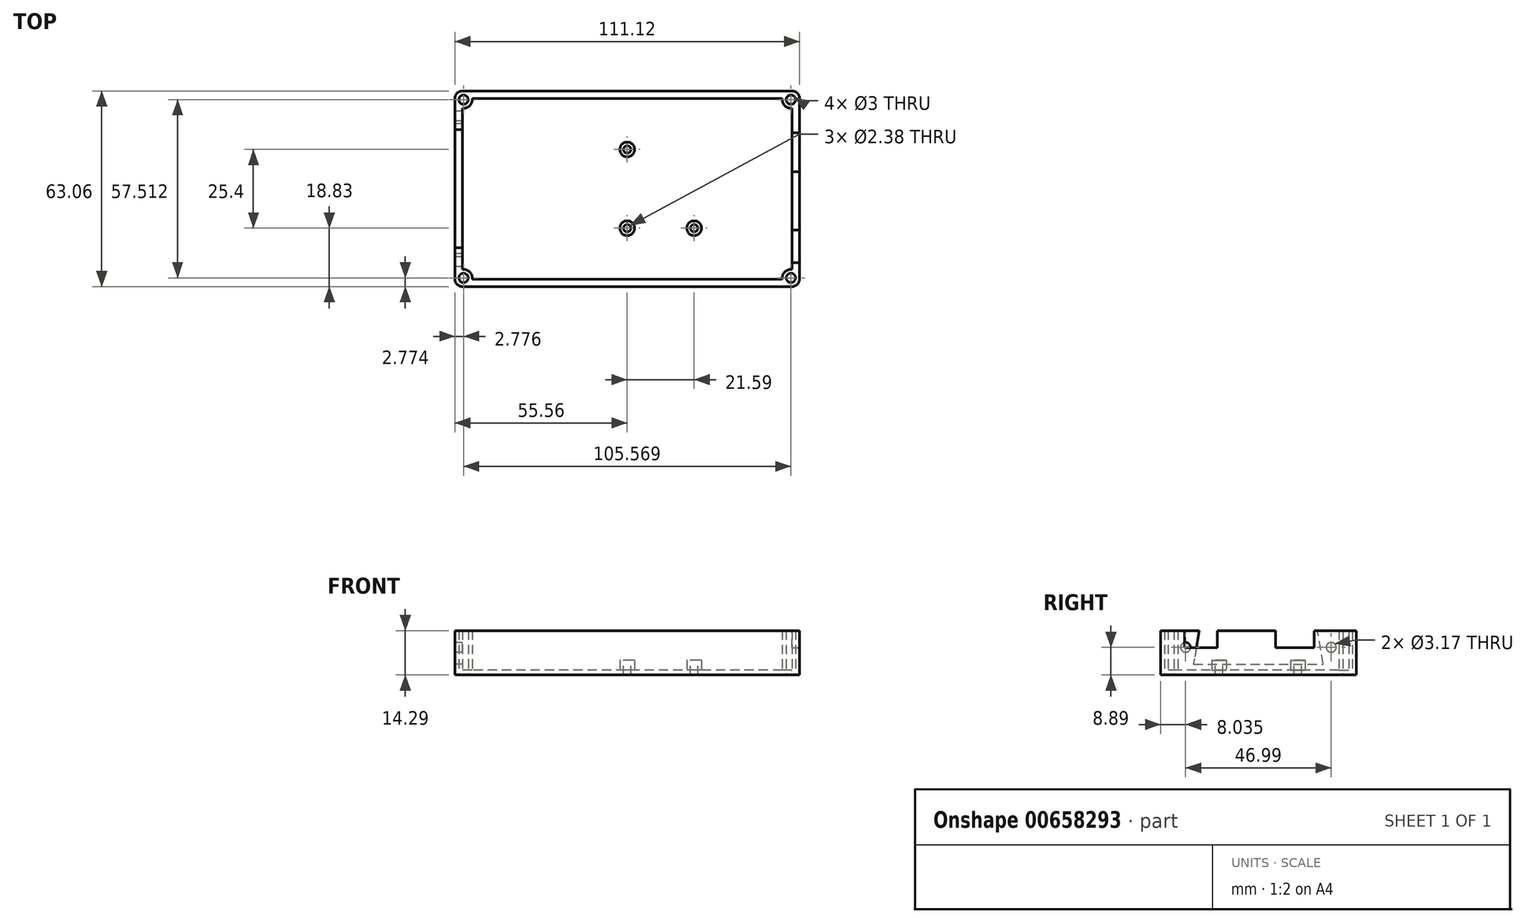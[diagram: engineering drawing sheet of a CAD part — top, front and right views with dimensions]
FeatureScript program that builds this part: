
annotation { "Feature Type Name" : "Feature", "Feature Type Description" : "" }
export const myFeature = defineFeature(function(context is Context, id is Id, definition is map)
    precondition{}
    {
        {
            var Q0;
            Q0=qCreatedBy(makeId("Top.planeOp"),FACE);
            var sketch = newSketch(context, id + "F0", { "sketchPlane" : qUnion([Q0])});
            skLineSegment(sketch, "E0.bottom", {"start": v(50.8, 26.77) * mm, "end": v(-50.8, 26.77) * mm});
            skLineSegment(sketch, "E0.top", {"start": v(50.8, -26.77) * mm, "end": v(-50.8, -26.77) * mm});
            skLineSegment(sketch, "E0.left", {"start": v(50.8, 26.77) * mm, "end": v(50.8, -26.77) * mm});
            skLineSegment(sketch, "E0.right", {"start": v(-50.8, 26.77) * mm, "end": v(-50.8, -26.77) * mm});
            skPoint(sketch, "E0.middle", {"position": v(0, 0) * mm});
            skSolve(sketch);
        }
        {
            var Q0;
            Q0=qCreatedBy(makeId("Top.planeOp"),FACE);
            var sketch = newSketch(context, id + "F1", { "sketchPlane" : qUnion([Q0])});
            skLineSegment(sketch, "E1.bottom", {"start": v(55.56, 31.53) * mm, "end": v(-55.56, 31.53) * mm});
            skLineSegment(sketch, "E1.top", {"start": v(55.56, -31.53) * mm, "end": v(-55.56, -31.53) * mm});
            skLineSegment(sketch, "E1.left", {"start": v(55.56, 31.53) * mm, "end": v(55.56, -31.53) * mm});
            skLineSegment(sketch, "E1.right", {"start": v(-55.56, 31.53) * mm, "end": v(-55.56, -31.53) * mm});
            skPoint(sketch, "E1.middle", {"position": v(0, 0) * mm});
            skLineSegment(sketch, "E2.bottom", {"start": v(53.97, 29.95) * mm, "end": v(-53.98, 29.95) * mm, "construction": true});
            skLineSegment(sketch, "E2.top", {"start": v(53.98, -29.95) * mm, "end": v(-53.97, -29.95) * mm, "construction": true});
            skLineSegment(sketch, "E2.left", {"start": v(53.97, 29.95) * mm, "end": v(53.98, -29.95) * mm, "construction": true});
            skLineSegment(sketch, "E2.right", {"start": v(-53.98, 29.95) * mm, "end": v(-53.97, -29.95) * mm, "construction": true});
            skSolve(sketch);
        }
        {
            var Q0;
            Q0=makeQuery(id+"F1.imprint","IMPRINT",FACE,{"disambiguationData":[TD([[makeQuery(id+"F1.imprint","IMPRINT",EDGE,{"derivedFrom":sQuery(id+"F1.wireOp",EDGE,"E1.bottom")}),1.0]])]});
            extrude(context, id + "F2", {"entities" : qUnion([Q0]), "depth" : 1.59 * mm, "offsetDistance" : 25.4 * mm});
        }
        {
            var Q0;
            Q0=makeQuery(id+"F2.opExtrude","CAP_FACE",FACE,{"disambiguationData":[OSD([sQuery(id+"F1.wireOp",EDGE,"E1.bottom"),sQuery(id+"F1.wireOp",EDGE,"E1.top"),sQuery(id+"F1.wireOp",EDGE,"E1.left"),sQuery(id+"F1.wireOp",EDGE,"E1.right")])],"isStart":false});
            var sketch = newSketch(context, id + "F3", { "sketchPlane" : qUnion([Q0])});
            skLineSegment(sketch, "E3.bottom", {"start": v(55.56, 31.53) * mm, "end": v(-55.56, 31.53) * mm});
            skLineSegment(sketch, "E3.top", {"start": v(55.56, -31.53) * mm, "end": v(-55.56, -31.53) * mm});
            skLineSegment(sketch, "E3.left", {"start": v(55.56, 31.53) * mm, "end": v(55.56, -31.53) * mm});
            skLineSegment(sketch, "E3.right", {"start": v(-55.56, 31.53) * mm, "end": v(-55.56, -31.53) * mm});
            skPoint(sketch, "E3.middle", {"position": v(0, 0) * mm});
            skLineSegment(sketch, "E4.left", {"start": v(53.18, 25.98) * mm, "end": v(53.18, -25.98) * mm});
            skLineSegment(sketch, "E4.right", {"start": v(-53.18, 25.98) * mm, "end": v(-53.18, -25.98) * mm});
            skArc(sketch, "E5", {"start": v(-52.78, 25.98) * mm, "mid": v(-50.82, 26.8) * mm, "end": v(-50, 28.76) * mm});
            skCircle(sketch, "E6", {"center": v(-52.78, 28.76) * mm, "radius": 1.5 * mm});
            skLineSegment(sketch, "E7", {"start": v(-50, 28.76) * mm, "end": v(-50, 29.15) * mm});
            skLineSegment(sketch, "E8", {"start": v(-52.78, 25.98) * mm, "end": v(-53.18, 25.98) * mm});
            skLineSegment(sketch, "E9", {"start": v(-55.56, 31.53) * mm, "end": v(-50.82, 26.8) * mm, "construction": true});
            skPoint(sketch, "E10", {"position": v(-53.2, 29.16) * mm});
            skPoint(sketch, "E11.orphan", {"position": v(-53.18, 37.1) * mm});
            skCircle(sketch, "E12.MirrorC", {"center": v(-52.78, -28.76) * mm, "radius": 1.5 * mm});
            skLineSegment(sketch, "E13.MirrorCS", {"start": v(-52.78, -25.98) * mm, "end": v(-53.18, -25.98) * mm});
            skArc(sketch, "E14.MirrorCS", {"start": v(-52.78, -25.98) * mm, "mid": v(-50.82, -26.8) * mm, "end": v(-50, -28.76) * mm});
            skLineSegment(sketch, "E15.MirrorCS", {"start": v(-50, -28.76) * mm, "end": v(-50, -29.15) * mm});
            skCircle(sketch, "E16.MirrorC", {"center": v(52.78, 28.76) * mm, "radius": 1.5 * mm});
            skLineSegment(sketch, "E17.MirrorCS", {"start": v(50, 28.76) * mm, "end": v(50, 29.15) * mm});
            skArc(sketch, "E18.MirrorCS", {"start": v(52.78, 25.98) * mm, "mid": v(50.82, 26.8) * mm, "end": v(50, 28.76) * mm});
            skLineSegment(sketch, "E19.MirrorCS", {"start": v(52.78, 25.98) * mm, "end": v(53.18, 25.98) * mm});
            skCircle(sketch, "E20.MirrorC", {"center": v(52.78, -28.76) * mm, "radius": 1.5 * mm});
            skLineSegment(sketch, "E21.MirrorCS", {"start": v(52.78, -25.98) * mm, "end": v(53.18, -25.98) * mm});
            skArc(sketch, "E22.MirrorCS", {"start": v(52.78, -25.98) * mm, "mid": v(50.82, -26.8) * mm, "end": v(50, -28.76) * mm});
            skLineSegment(sketch, "E23.MirrorCS", {"start": v(50, -28.76) * mm, "end": v(50, -29.15) * mm});
            skPoint(sketch, "E24.orphan", {"position": v(-53.18, -36.9) * mm});
            skLineSegment(sketch, "E25.trimOffspring", {"start": v(50, -29.15) * mm, "end": v(-50, -29.15) * mm});
            skPoint(sketch, "E26.orphan", {"position": v(53.18, -37.1) * mm});
            skLineSegment(sketch, "E27.trimOffspring", {"start": v(50, 29.15) * mm, "end": v(-50, 29.15) * mm});
            skPoint(sketch, "E28.orphan", {"position": v(53.18, 36.9) * mm});
            skSolve(sketch);
        }
        {
            var Q0;
            Q0=qSketchRegion(id+"F3",true);
            extrude(context, id + "F4", {"entities" : qUnion([Q0]), "operationType" : NewBodyOperationType.ADD, "depth" : 12.7 * mm, "offsetDistance" : 25.4 * mm});
        }
        {
            var Q0;
            Q0=makeQuery(id+"F4.boolean.opBoolean","MERGE",EDGE,{"derivedFrom":[makeQuery(id+"F2.opExtrude","SWEPT_EDGE",EDGE,{"disambiguationData":[OSD([sQuery(id+"F1.wireOp",EDGE,"E1.top"),sQuery(id+"F1.wireOp",EDGE,"E1.left")])]}),makeQuery(id+"F4.opExtrude","SWEPT_EDGE",EDGE,{"disambiguationData":[OSD([sQuery(id+"F3.wireOp",EDGE,"E3.top"),sQuery(id+"F3.wireOp",EDGE,"E3.left")])]})]});
            var Q1;
            Q1=makeQuery(id+"F4.boolean.opBoolean","MERGE",EDGE,{"derivedFrom":[makeQuery(id+"F2.opExtrude","SWEPT_EDGE",EDGE,{"disambiguationData":[OSD([sQuery(id+"F1.wireOp",EDGE,"E1.bottom"),sQuery(id+"F1.wireOp",EDGE,"E1.left")])]}),makeQuery(id+"F4.opExtrude","SWEPT_EDGE",EDGE,{"disambiguationData":[OSD([sQuery(id+"F3.wireOp",EDGE,"E3.bottom"),sQuery(id+"F3.wireOp",EDGE,"E3.left")])]})]});
            var Q2;
            Q2=makeQuery(id+"F4.boolean.opBoolean","MERGE",EDGE,{"derivedFrom":[makeQuery(id+"F2.opExtrude","SWEPT_EDGE",EDGE,{"disambiguationData":[OSD([sQuery(id+"F1.wireOp",EDGE,"E1.top"),sQuery(id+"F1.wireOp",EDGE,"E1.right")])]}),makeQuery(id+"F4.opExtrude","SWEPT_EDGE",EDGE,{"disambiguationData":[OSD([sQuery(id+"F3.wireOp",EDGE,"E3.top"),sQuery(id+"F3.wireOp",EDGE,"E3.right")])]})]});
            var Q3;
            Q3=makeQuery(id+"F4.boolean.opBoolean","MERGE",EDGE,{"derivedFrom":[makeQuery(id+"F2.opExtrude","SWEPT_EDGE",EDGE,{"disambiguationData":[OSD([sQuery(id+"F1.wireOp",EDGE,"E1.bottom"),sQuery(id+"F1.wireOp",EDGE,"E1.right")])]}),makeQuery(id+"F4.opExtrude","SWEPT_EDGE",EDGE,{"disambiguationData":[OSD([sQuery(id+"F3.wireOp",EDGE,"E3.bottom"),sQuery(id+"F3.wireOp",EDGE,"E3.right")])]})]});
            fillet(context, id + "F5", {"entities" : qUnion([Q0, Q1, Q2, Q3]), "radius" : 2.38 * mm, "tangentPropagation" : true, "allowEdgeOverflow" : false});
        }
        {
            var Q0;
            Q0=makeQuery(id+"F4.boolean.opBoolean","MERGE",FACE,{"derivedFrom":[makeQuery(id+"F2.opExtrude","SWEPT_FACE",FACE,{"disambiguationData":[OSD([sQuery(id+"F1.wireOp",EDGE,"E1.left")])]}),makeQuery(id+"F4.opExtrude","SWEPT_FACE",FACE,{"disambiguationData":[OSD([sQuery(id+"F3.wireOp",EDGE,"E3.left")])]})]});
            var sketch = newSketch(context, id + "F6", { "sketchPlane" : qUnion([Q0])});
            skLineSegment(sketch, "E29.bottom", {"start": v(-23.77, 14.29) * mm, "end": v(-13.27, 14.29) * mm});
            skLineSegment(sketch, "E29.top", {"start": v(-23.77, 8.76) * mm, "end": v(-13.27, 8.76) * mm});
            skLineSegment(sketch, "E29.left", {"start": v(-23.77, 14.29) * mm, "end": v(-23.77, 8.76) * mm});
            skLineSegment(sketch, "E29.right", {"start": v(-13.27, 14.29) * mm, "end": v(-13.27, 8.76) * mm});
            skLineSegment(sketch, "E30.bottom", {"start": v(5.52, 14.29) * mm, "end": v(18.02, 14.29) * mm});
            skLineSegment(sketch, "E30.top", {"start": v(5.52, 8.76) * mm, "end": v(18.02, 8.76) * mm});
            skLineSegment(sketch, "E30.left", {"start": v(5.52, 14.29) * mm, "end": v(5.52, 8.76) * mm});
            skLineSegment(sketch, "E30.right", {"start": v(18.02, 14.29) * mm, "end": v(18.02, 8.76) * mm});
            skLineSegment(sketch, "E31", {"start": v(-26.77, 14.29) * mm, "end": v(-26.77, 0) * mm, "construction": true});
            skLineSegment(sketch, "E32.MirrorCS", {"start": v(26.77, 14.29) * mm, "end": v(26.77, 0) * mm, "construction": true});
            skPoint(sketch, "E33", {"position": v(11.77, 8.76) * mm});
            skSolve(sketch);
        }
        {
            var Q0;
            Q0=qSketchRegion(id+"F6",true);
            extrude(context, id + "F7", {"entities" : qUnion([Q0]), "operationType" : NewBodyOperationType.REMOVE, "endBound" : BoundingType.UP_TO_NEXT, "oppositeDirection" : true, "depth" : 25.4 * mm, "offsetDistance" : 25.4 * mm});
        }
        {
            var Q0;
            Q0=makeQuery(id+"F0.imprint","IMPRINT",FACE,{"disambiguationData":[TD([[makeQuery(id+"F0.imprint","IMPRINT",EDGE,{"derivedFrom":sQuery(id+"F0.wireOp",EDGE,"E0.bottom")}),1.0]])]});
            var sketch = newSketch(context, id + "F8", { "sketchPlane" : qUnion([Q0])});
            skLineSegment(sketch, "E34.bottom", {"start": v(-42.55, -25.36) * mm, "end": v(33.02, -25.36) * mm});
            skLineSegment(sketch, "E34.top", {"start": v(-42.55, -22.18) * mm, "end": v(33.02, -22.18) * mm});
            skLineSegment(sketch, "E34.left", {"start": v(-42.55, -25.36) * mm, "end": v(-42.55, -22.18) * mm});
            skLineSegment(sketch, "E34.right", {"start": v(33.02, -25.36) * mm, "end": v(33.02, -22.18) * mm});
            skPoint(sketch, "E35", {"position": v(-42.55, -23.77) * mm});
            skLineSegment(sketch, "E36.MirrorCS", {"start": v(33.02, 25.36) * mm, "end": v(33.02, 22.18) * mm});
            skLineSegment(sketch, "E37.MirrorCS", {"start": v(-42.55, 25.36) * mm, "end": v(-42.55, 22.18) * mm});
            skLineSegment(sketch, "E38.MirrorCS", {"start": v(-42.55, 22.18) * mm, "end": v(33.02, 22.18) * mm});
            skLineSegment(sketch, "E39.MirrorCS", {"start": v(-42.55, 25.36) * mm, "end": v(33.02, 25.36) * mm});
            skPoint(sketch, "E40.MirrorP", {"position": v(-42.55, 23.77) * mm});
            skSolve(sketch);
        }
        {
            var Q0;
            Q0=makeQuery(id+"F4.boolean.opBoolean","MERGE",FACE,{"derivedFrom":[makeQuery(id+"F2.opExtrude","SWEPT_FACE",FACE,{"disambiguationData":[OSD([sQuery(id+"F1.wireOp",EDGE,"E1.right")])]}),makeQuery(id+"F4.opExtrude","SWEPT_FACE",FACE,{"disambiguationData":[OSD([sQuery(id+"F3.wireOp",EDGE,"E3.right")])]})]});
            var sketch = newSketch(context, id + "F9", { "sketchPlane" : qUnion([Q0])});
            skLineSegment(sketch, "E41", {"start": v(-19.05, 14.29) * mm, "end": v(19.05, 14.29) * mm});
            skLineSegment(sketch, "E42", {"start": v(19.05, 14.29) * mm, "end": v(20.95, 3.5) * mm});
            skLineSegment(sketch, "E43", {"start": v(20.95, 3.5) * mm, "end": v(-20.96, 3.5) * mm});
            skLineSegment(sketch, "E44", {"start": v(-20.96, 3.5) * mm, "end": v(-19.05, 14.29) * mm});
            skPoint(sketch, "E45", {"position": v(0, 14.29) * mm});
            skPoint(sketch, "E46", {"position": v(0, 3.5) * mm});
            skCircle(sketch, "E47", {"center": v(-23.5, 8.9) * mm, "radius": 1.59 * mm});
            skCircle(sketch, "E48", {"center": v(23.5, 8.9) * mm, "radius": 1.59 * mm});
            skLineSegment(sketch, "E49", {"start": v(0, 14.29) * mm, "end": v(0, 3.5) * mm, "construction": true});
            skPoint(sketch, "E50", {"position": v(0, 8.89) * mm});
            skSolve(sketch);
        }
        {
            var Q0;
            Q0=qSketchRegion(id+"F9",true);
            extrude(context, id + "F10", {"entities" : qUnion([Q0]), "operationType" : NewBodyOperationType.REMOVE, "endBound" : BoundingType.UP_TO_NEXT, "oppositeDirection" : true, "depth" : 25.4 * mm, "offsetDistance" : 25.4 * mm});
        }
        {
            var Q0;
            Q0=makeQuery(id+"F4.boolean.opBoolean","SPLIT",FACE,{"disambiguationData":[TD([makeQuery(id+"F4.opExtrude","SWEPT_FACE",FACE,{"disambiguationData":[OSD([sQuery(id+"F3.wireOp",EDGE,"E4.left")])]})])],"derivedFrom":makeQuery(id+"F2.opExtrude","CAP_FACE",FACE,{"disambiguationData":[OSD([sQuery(id+"F1.wireOp",EDGE,"E1.bottom"),sQuery(id+"F1.wireOp",EDGE,"E1.top"),sQuery(id+"F1.wireOp",EDGE,"E1.left"),sQuery(id+"F1.wireOp",EDGE,"E1.right")])],"isStart":false})});
            var sketch = newSketch(context, id + "F11", { "sketchPlane" : qUnion([Q0])});
            skCircle(sketch, "E51", {"center": v(0, 12.7) * mm, "radius": 2.38 * mm});
            skCircle(sketch, "E52.MirrorC", {"center": v(0, -12.7) * mm, "radius": 2.38 * mm});
            skCircle(sketch, "E53", {"center": v(21.59, -12.7) * mm, "radius": 2.38 * mm});
            skSolve(sketch);
        }
        {
            var Q0;
            Q0=qSketchRegion(id+"F11",true);
            extrude(context, id + "F12", {"entities" : qUnion([Q0]), "operationType" : NewBodyOperationType.ADD, "depth" : 3.17 * mm, "offsetDistance" : 25.4 * mm});
        }
        {
            var Q0;
            Q0=makeQuery(id+"F12.opExtrude","CAP_FACE",FACE,{"disambiguationData":[OSD([sQuery(id+"F11.wireOp",EDGE,"E51")])],"isStart":false});
            var sketch = newSketch(context, id + "F13", { "sketchPlane" : qUnion([Q0])});
            skCircle(sketch, "E54", {"center": v(0, 12.7) * mm, "radius": 1.2 * mm});
            skCircle(sketch, "E55.MirrorC", {"center": v(0, -12.7) * mm, "radius": 1.2 * mm});
            skCircle(sketch, "E56", {"center": v(21.59, -12.7) * mm, "radius": 1.2 * mm});
            skSolve(sketch);
        }
        {
            var Q0;
            Q0=qSketchRegion(id+"F13",true);
            extrude(context, id + "F14", {"entities" : qUnion([Q0]), "operationType" : NewBodyOperationType.REMOVE, "endBound" : BoundingType.THROUGH_ALL, "oppositeDirection" : true, "depth" : 25.4 * mm, "offsetDistance" : 25.4 * mm});
        }
        {
            var Q0;
            {var subQ0=sQuery(id+"F3.wireOp",EDGE,"E6");var subQ2=sQuery(id+"F3.wireOp",EDGE,"E5");var subQ4=sQuery(id+"F3.wireOp",EDGE,"E4.right");var subQ6=sQuery(id+"F3.wireOp",EDGE,"E4.left");var subQ8=sQuery(id+"F3.wireOp",EDGE,"E3.right");var subQ10=sQuery(id+"F1.wireOp",EDGE,"E1.bottom");var subQ11=makeQuery(id+"F2.opExtrude","SWEPT_FACE",FACE,{"disambiguationData":[OSD([subQ10])]});var subQ12=sQuery(id+"F3.wireOp",EDGE,"E19.MirrorCS");var subQ14=sQuery(id+"F3.wireOp",EDGE,"E3.bottom");var subQ17=sQuery(id+"F3.wireOp",EDGE,"E3.left");var subQ23=sQuery(id+"F3.wireOp",EDGE,"E7");var subQ25=sQuery(id+"F3.wireOp",EDGE,"E8");var subQ28=sQuery(id+"F3.wireOp",EDGE,"E16.MirrorC");var subQ30=sQuery(id+"F3.wireOp",EDGE,"E17.MirrorCS");var subQ32=sQuery(id+"F3.wireOp",EDGE,"E18.MirrorCS");var subQ35=sQuery(id+"F3.wireOp",EDGE,"E27.trimOffspring");var subQ37=sQuery(id+"F3.wireOp",EDGE,"E15.MirrorCS");var subQ38=sQuery(id+"F3.wireOp",EDGE,"E14.MirrorCS");var subQ39=sQuery(id+"F3.wireOp",EDGE,"E13.MirrorCS");var subQ40=sQuery(id+"F3.wireOp",EDGE,"E12.MirrorC");var subQ41=sQuery(id+"F3.wireOp",EDGE,"E3.top");var subQ43=sQuery(id+"F3.wireOp",EDGE,"E22.MirrorCS");var subQ44=sQuery(id+"F3.wireOp",EDGE,"E25.trimOffspring");var subQ45=sQuery(id+"F3.wireOp",EDGE,"E23.MirrorCS");var subQ46=sQuery(id+"F3.wireOp",EDGE,"E20.MirrorC");var subQ47=sQuery(id+"F3.wireOp",EDGE,"E21.MirrorCS");Q0=makeQuery(id+"F10.boolean.opBoolean","SPLIT",FACE,{"disambiguationData":[TD([subQ11])],"derivedFrom":makeQuery(id+"F7.boolean.opBoolean","SPLIT",FACE,{"disambiguationData":[TD([subQ11])],"derivedFrom":makeQuery(id+"F4.opExtrude","CAP_FACE",FACE,{"disambiguationData":[OSD([subQ14,subQ41,subQ17,subQ8,subQ6,subQ4,subQ2,subQ0,subQ23,subQ25,subQ40,subQ39,subQ38,subQ37,subQ28,subQ30,subQ32,subQ12,subQ46,subQ47,subQ43,subQ45,subQ44,subQ35])],"isStart":false})})});}
            var sketch = newSketch(context, id + "F15", { "sketchPlane" : qUnion([Q0])});
            skCircle(sketch, "E57.0", {"center": v(52.78, 28.76) * mm, "radius": 1.5 * mm});
            skCircle(sketch, "E58.0", {"center": v(52.78, -28.76) * mm, "radius": 1.5 * mm});
            skCircle(sketch, "E59.0", {"center": v(-52.78, -28.76) * mm, "radius": 1.5 * mm});
            skCircle(sketch, "E60.0", {"center": v(-52.78, 28.76) * mm, "radius": 1.5 * mm});
            skSolve(sketch);
        }
        {
            var Q0;
            Q0=qSketchRegion(id+"F15",true);
            extrude(context, id + "F16", {"entities" : qUnion([Q0]), "operationType" : NewBodyOperationType.REMOVE, "endBound" : BoundingType.THROUGH_ALL, "oppositeDirection" : true, "depth" : 25.4 * mm, "offsetDistance" : 25.4 * mm});
        }
    });
